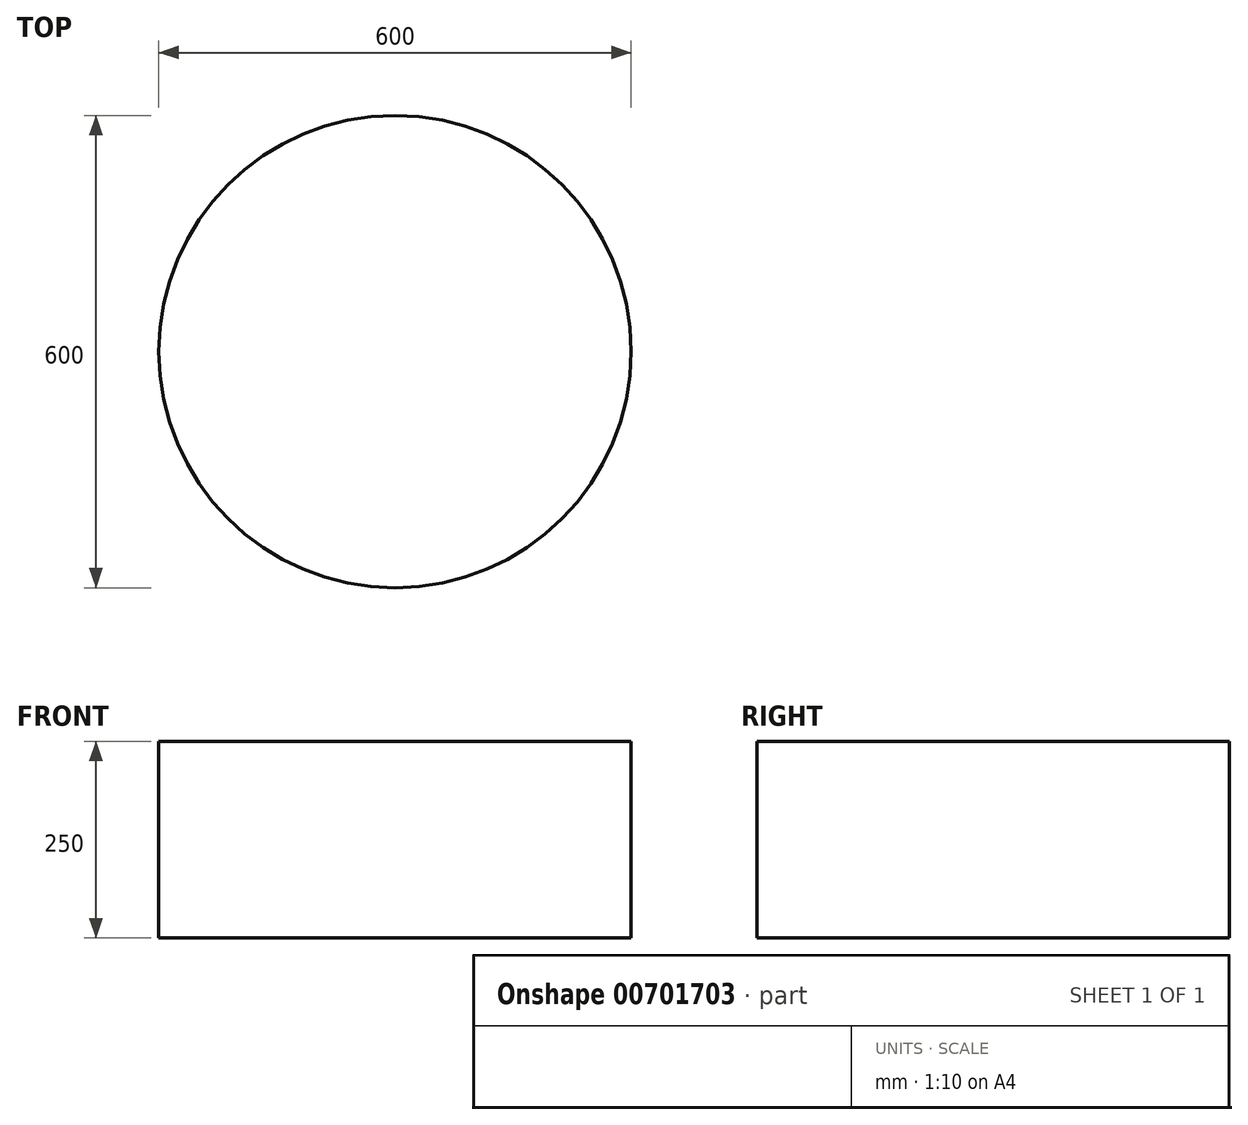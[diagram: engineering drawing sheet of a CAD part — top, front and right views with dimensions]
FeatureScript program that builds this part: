
annotation { "Feature Type Name" : "Feature", "Feature Type Description" : "" }
export const myFeature = defineFeature(function(context is Context, id is Id, definition is map)
    precondition{}
    {
        {
            var Q0;
            Q0=qCreatedBy(makeId("Top.planeOp"),FACE);
            var sketch = newSketch(context, id + "F0", { "sketchPlane" : qUnion([Q0])});
            skCircle(sketch, "E0", {"center": v(0, 0) * mm, "radius": 300 * mm});
            skSolve(sketch);
        }
        {
            var Q0;
            Q0 = qSketchRegion(id + "F0", true);
            extrude(context, id + "F1", {"entities" : qUnion([Q0]), "depth" : 250 * mm, "offsetDistance" : 25 * mm});
        }
    });
